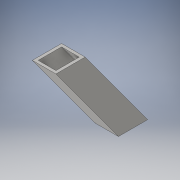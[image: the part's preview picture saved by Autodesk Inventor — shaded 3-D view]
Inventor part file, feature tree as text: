
AUTODESK INVENTOR PART (.ipt)
format: ipt  version: 2016 (Build 200138000, 138)  size: 107,520 bytes
history: native  units: in
note: dims shown in document units (in); Inventor stores cm internally (conversion verified against a paired STEP export)
features: sketch x3, extrude x1, sweep x1
ambient origin geometry x8: Origin, YZ Plane, XZ Plane, XY Plane, X Axis, Y Axis, Z Axis, Center Point
bodies: Solid1 (feature_tree)
feature tree (5):
  extrude  "Extrusion1"  Depth=1.0in
  sweep  "Sweep2"
  sketch  "Sketch1"  dims[d0=0.3697in d2=1.0in]
  sketch  "Sketch3"  dims[d3=3.625in d4=1.0in d5=0.0in d10=0.75in d12=0.125in d13=0.125in d16=0.125in d17=0.0in d18=0.0in]
  sketch  "3D Sketch1"
